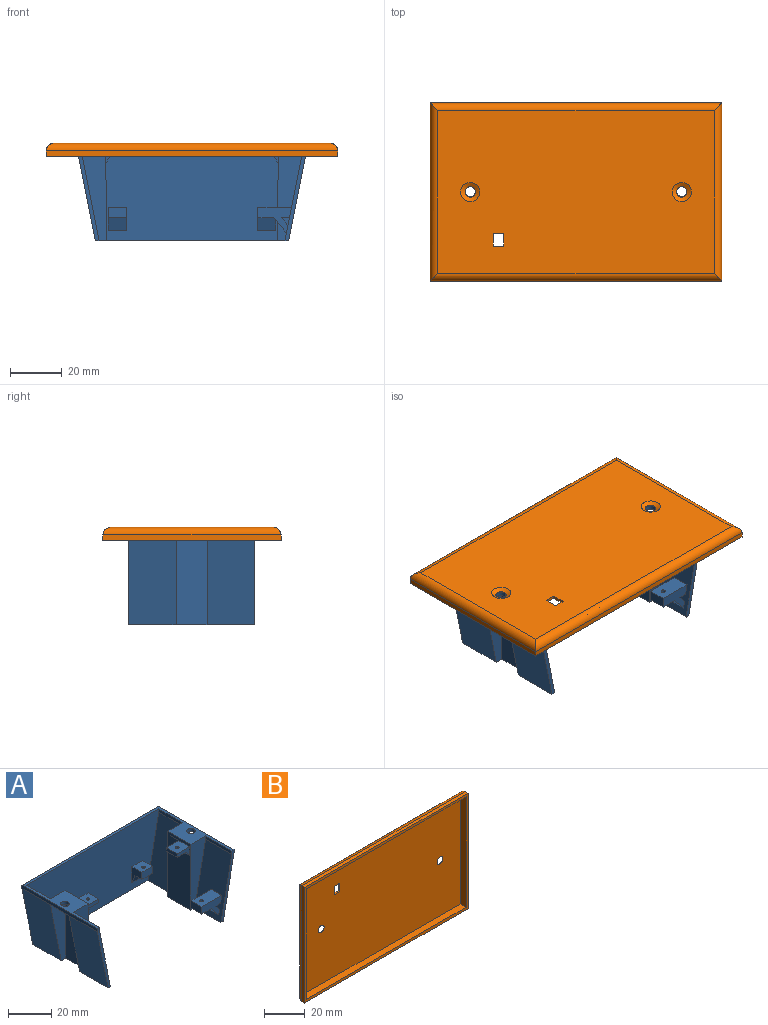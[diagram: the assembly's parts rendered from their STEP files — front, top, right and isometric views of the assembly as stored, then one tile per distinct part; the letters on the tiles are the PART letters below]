
ASSEMBLY  parts=2 mates=1
PART A: 75 faces, bbox 89x49x36.8 mm
  f0: plane 7x5.97mm, normal (0,0,-1), area 39.5mm2, adj f69,f70,f71,f72,f74
  f1: plane 35x15mm, normal (-1,0,0.01), area 490.5mm2, adj f8,f9,f10,f25,f62,f64,f68
  f2: plane 86x36.8mm, normal (0,-1,0), area 2793.8mm2, adj f7,f19,f21,f25,f31,f32,f40,f43
  f3: plane 35x17mm, normal (-0.98,0,0.2), area 557.2mm2, adj f4,f10,f11,f12,f25,f52,f54,f57
  f4: plane 7x3.15mm, normal (0,0,-1), area 22mm2, adj f3,f52,f54,f58
  f5: plane 12x9.5mm, normal (0,0,-1), area 101.4mm2, adj f13,f20,f27,f28,f29
  f6: plane 12x9.5mm, normal (0,0,-1), area 101.4mm2, adj f15,f24,f36,f37,f38
  f7: plane 15.5x1.8mm, normal (-1,0,0), area 27.9mm2, adj f2,f8,f19,f31
  f8: plane 36.8x10mm, normal (0,1,0), area 235.9mm2, adj f1,f7,f9,f19,f25,f31
  f9: plane 15x1.8mm, normal (-1,0,0), area 27mm2, adj f1,f8,f10,f19,f67
  f10: plane 36.8x10mm, normal (0,-1,0), area 235.9mm2, adj f1,f3,f9,f11,f19,f25
  f11: plane 17x1.8mm, normal (-1,0,0), area 30.6mm2, adj f3,f10,f12,f19
  f12: plane 36.8x8.5mm, normal (0,-1,0), area 55.2mm2, adj f3,f11,f13,f19,f25,f30
  f13: plane 49x1.8mm, normal (1,0,0), area 88.2mm2, adj f5,f12,f14,f19,f26,f30
  f14: plane 89x36.8mm, normal (0,1,0), area 3030.2mm2, adj f13,f15,f19,f25,f26,f39
  f15: plane 49x1.8mm, normal (-1,0,0), area 88.2mm2, adj f6,f14,f16,f19,f35,f39
  f16: plane 36.8x8.5mm, normal (0,-1,0), area 55.2mm2, adj f15,f17,f19,f25,f34,f35
  f17: plane 17x1.8mm, normal (1,0,0), area 30.6mm2, adj f16,f18,f19,f34
  f18: plane 36.8x10mm, normal (0,-1,0), area 235.9mm2, adj f17,f19,f22,f25,f33,f34
  f19: plane 89x49mm, normal (0,0,1), area 535.9mm2, adj f2,f7,f8,f9,f10,f11,f12,f13
  f20: cylinder r=2mm len=4mm, axis (0,0,1), area 22.6mm2, adj f5,f19
  f21: plane 15.5x1.8mm, normal (1,0,0), area 27.9mm2, adj f2,f19,f23,f32
  f22: plane 15x1.8mm, normal (1,0,0), area 27mm2, adj f18,f19,f23,f33,f73
  f23: plane 36.8x10mm, normal (0,1,0), area 235.8mm2, adj f19,f21,f22,f25,f32,f33
  f24: cylinder r=2mm len=4mm, axis (0,0,1), area 22.6mm2, adj f6,f19
  f25: plane 75x49mm, normal (0,0,-1), area 273mm2, adj f1,f2,f3,f8,f10,f12,f14,f16
  f26: plane 35x18.5mm, normal (0.98,0,-0.2), area 660.3mm2, adj f13,f14,f25,f27
  f27: plane 35x10mm, normal (0,-1,0), area 218.7mm2, adj f5,f25,f26,f28
  f28: plane 35x12mm, normal (1,0,-0.01), area 420mm2, adj f5,f25,f27,f29
  f29: plane 35x10mm, normal (0,1,0), area 218.8mm2, adj f5,f25,f28,f30
  f30: plane 35x18.5mm, normal (0.98,0,-0.2), area 660.3mm2, adj f12,f13,f25,f29
  f31: plane 35x15.5mm, normal (-0.98,0,0.2), area 553.2mm2, adj f2,f7,f8,f25
  f32: plane 35x15.5mm, normal (0.98,0,0.2), area 553.2mm2, adj f2,f21,f23,f25
  f33: plane 35x15mm, normal (1,0,0.01), area 490.5mm2, adj f18,f22,f23,f25,f69,f70,f74
  f34: plane 35x17mm, normal (0.98,0,0.2), area 606.8mm2, adj f16,f17,f18,f25
  f35: plane 35x18.5mm, normal (-0.98,0,-0.2), area 660.3mm2, adj f15,f16,f25,f36
  f36: plane 35x10mm, normal (0,1,0), area 218.7mm2, adj f6,f25,f35,f37
  f37: plane 35x12mm, normal (-1,0,-0.01), area 420mm2, adj f6,f25,f36,f38
  f38: plane 35x10mm, normal (0,-1,0), area 218.8mm2, adj f6,f25,f37,f39
  f39: plane 35x18.5mm, normal (-0.98,0,-0.2), area 660.3mm2, adj f14,f15,f25,f38
  f40: plane 9x6.5mm, normal (-1,0,0), area 31mm2, adj f2,f41,f44,f45,f60
  f41: plane 7x4mm, normal (0,-1,0), area 28mm2, adj f40,f43,f44,f45
  f42: cylinder r=0.85mm len=4mm, axis (0,0,1), area 21.4mm2, adj f44,f45
  f43: plane 9x6.5mm, normal (1,0,0), area 31mm2, adj f2,f41,f44,f45,f60
  f44: plane 7x4.5mm, normal (0,0,-1), area 29.2mm2, adj f40,f41,f42,f43,f60
  f45: plane 7x6.5mm, normal (0,0,1), area 43.2mm2, adj f2,f40,f41,f42,f43
  f46: plane 7x4mm, normal (0,-1,0), area 28mm2, adj f47,f48,f50,f51
  f47: plane 9x6.5mm, normal (1,0,0), area 31mm2, adj f2,f46,f50,f51,f61
  f48: plane 9x6.5mm, normal (-1,0,0), area 31mm2, adj f2,f46,f50,f51,f61
  f49: cylinder r=0.85mm len=4mm, axis (0,0,1), area 21.4mm2, adj f50,f51
  f50: plane 7x4.5mm, normal (0,0,-1), area 29.2mm2, adj f46,f47,f48,f49,f61
  f51: plane 7x6.5mm, normal (0,0,1), area 43.2mm2, adj f2,f46,f47,f48,f49
  f52: plane 13.1x10.03mm, normal (0,1,0), area 64.5mm2, adj f3,f4,f53,f56,f57,f58,f59
  f53: plane 7x4mm, normal (-1,0,0), area 28mm2, adj f52,f54,f56,f57
  f54: plane 13.1x10.03mm, normal (0,-1,0), area 64.5mm2, adj f3,f4,f53,f56,f57,f58,f59
  f55: cylinder r=0.85mm len=4mm, axis (0,0,1), area 21.4mm2, adj f56,f57
  f56: plane 7x6.15mm, normal (0,0,-1), area 40.8mm2, adj f52,f53,f54,f55,f59
  f57: plane 13.1x7mm, normal (0,0,1), area 89.4mm2, adj f3,f52,f53,f54,f55
  f58: plane 7x3.09mm, normal (0.77,0,0.63), area 28mm2, adj f3,f4,f52,f54
  f59: plane 7x6.03mm, normal (-0.77,0,-0.63), area 54.6mm2, adj f3,f52,f54,f56
  f60: plane 7x5mm, normal (0,-0.93,-0.37), area 37.7mm2, adj f2,f40,f43,f44
  f61: plane 7x5mm, normal (0,-0.93,-0.37), area 37.7mm2, adj f2,f47,f48,f50
  f62: plane 8x4.94mm, normal (0,1,0), area 18.9mm2, adj f1,f63,f66,f67,f68
  f63: plane 7x2mm, normal (-1,0,0), area 14mm2, adj f62,f64,f66,f67
  f64: plane 8x4.94mm, normal (0,-1,0), area 18.9mm2, adj f1,f63,f66,f67,f68
  f65: cylinder r=0.85mm len=2mm, axis (0,0,1), area 10.7mm2, adj f66,f67
  f66: plane 7x5.97mm, normal (0,0,-1), area 39.5mm2, adj f62,f63,f64,f65,f68
  f67: plane 8x7mm, normal (0,0,1), area 53.7mm2, adj f9,f62,f63,f64,f65
  f68: plane 7x2.94mm, normal (-0.83,0,-0.55), area 24.7mm2, adj f1,f62,f64,f66
  f69: plane 8x4.94mm, normal (0,1,0), area 18.9mm2, adj f0,f33,f72,f73,f74
  f70: plane 8x4.94mm, normal (0,-1,0), area 18.9mm2, adj f0,f33,f72,f73,f74
  f71: cylinder r=0.85mm len=2mm, axis (0,0,1), area 10.7mm2, adj f0,f73
  f72: plane 7x2mm, normal (1,0,0), area 14mm2, adj f0,f69,f70,f73
  f73: plane 8x7mm, normal (0,0,1), area 53.7mm2, adj f22,f69,f70,f71,f72
  f74: plane 7x2.94mm, normal (0.83,0,-0.55), area 24.7mm2, adj f0,f33,f69,f70
PART B: 21 faces, bbox 113x5x69 mm
  f0: plane 69x2mm, normal (1,0,0), area 138mm2, adj f1,f3,f9,f11
  f1: plane 113x2mm, normal (0,0,1), area 226mm2, adj f0,f2,f9,f12
  f2: plane 69x2mm, normal (-1,0,0), area 138mm2, adj f1,f3,f9,f14
  f3: plane 113x2mm, normal (0,0,-1), area 226mm2, adj f0,f2,f9,f13
  f4: plane 107x63mm, normal (0,1,0), area 6633.5mm2, adj f11,f12,f13,f14,f15,f16,f17,f18
  f5: plane 66x4mm, normal (1,0,0), area 264mm2, adj f6,f8,f9,f10
  f6: plane 110x4mm, normal (0,0,-1), area 440mm2, adj f5,f7,f9,f10
  f7: plane 66x4mm, normal (-1,0,0), area 264mm2, adj f6,f8,f9,f10
  f8: plane 110x4mm, normal (0,0,1), area 440mm2, adj f5,f7,f9,f10
  f9: plane 113x69mm, normal (0,-1,0), area 537mm2, adj f0,f1,f2,f3,f5,f6,f7,f8
  f10: plane 110x66mm, normal (0,-1,0), area 7214.9mm2, adj f5,f6,f7,f8,f15,f16,f17,f18
  f11: cylinder r=3mm len=69mm, axis (0,0,1), area 314.9mm2, adj f0,f4,f12,f13
  f12: cylinder r=3mm len=113mm, axis (-1,0,0), area 522.2mm2, adj f1,f4,f11,f14
  f13: cylinder r=3mm len=113mm, axis (1,0,0), area 522.2mm2, adj f3,f4,f11,f14
  f14: cylinder r=3mm len=69mm, axis (0,0,-1), area 314.9mm2, adj f2,f4,f12,f13
  f15: cone r=2mm half-angle=60deg, axis (0,1,0), area 36mm2, adj f4,f10
  f16: cone r=2mm half-angle=60deg, axis (0,1,0), area 36mm2, adj f4,f10
  f17: plane 5x1mm, normal (-1,0,0), area 5mm2, adj f4,f10,f18,f20
  f18: plane 4x1mm, normal (0,0,1), area 4mm2, adj f4,f10,f17,f19
  f19: plane 5x1mm, normal (1,0,0), area 5mm2, adj f4,f10,f18,f20
  f20: plane 4x1mm, normal (0,0,-1), area 4mm2, adj f4,f10,f17,f19
PLACE A at identity fixed
PLACE B rot(axis=(1,0,0),90deg) t=(0,-0.18,2.8)mm
MATE planar A.f19 <-> B.f10  axis (0,0,1) through (0,5.72,1.8)mm
